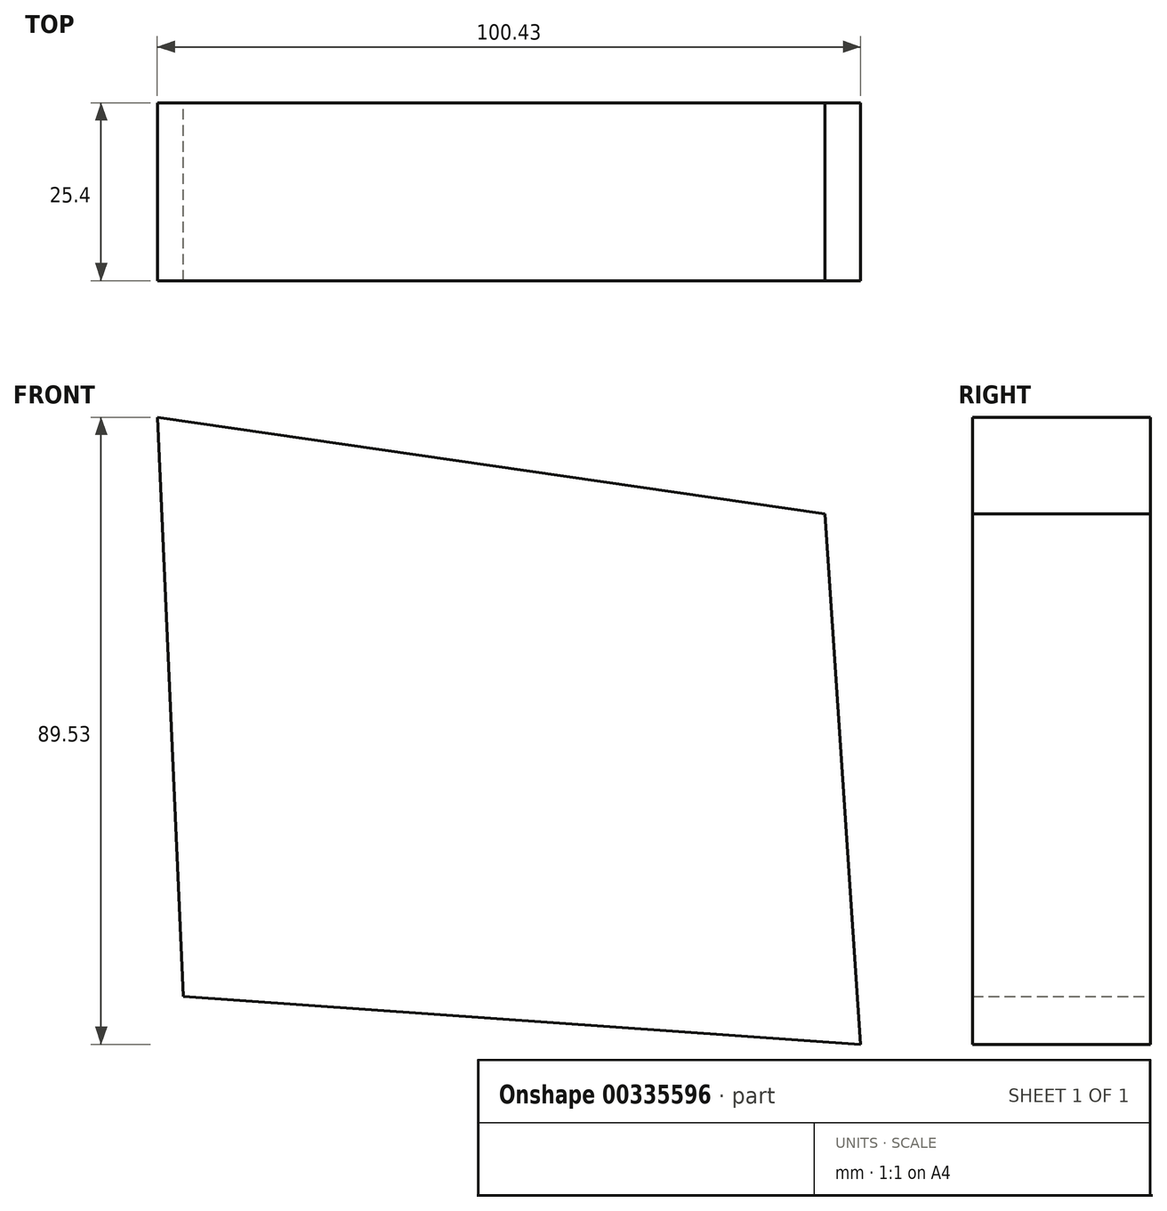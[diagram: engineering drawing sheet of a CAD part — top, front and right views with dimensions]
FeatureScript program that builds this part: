
annotation { "Feature Type Name" : "Feature", "Feature Type Description" : "" }
export const myFeature = defineFeature(function(context is Context, id is Id, definition is map)
    precondition{}
    {
        {
            var Q0;
            Q0=qCreatedBy(makeId("Front.planeOp"),FACE);
            var sketch = newSketch(context, id + "F0", { "sketchPlane" : qUnion([Q0])});
            skLineSegment(sketch, "E0", {"start": v(-48.03, 50.98) * mm, "end": v(-44.34, -31.73) * mm});
            skLineSegment(sketch, "E1", {"start": v(-44.34, -31.73) * mm, "end": v(52.4, -38.55) * mm});
            skLineSegment(sketch, "E2", {"start": v(52.4, -38.55) * mm, "end": v(47.32, 37.19) * mm});
            skLineSegment(sketch, "E3", {"start": v(47.32, 37.19) * mm, "end": v(-48.03, 50.98) * mm});
            skSolve(sketch);
        }
        {
            var Q0;
            Q0=makeQuery(id+"F0.imprint","IMPRINT",FACE,{"disambiguationData":[TD([[makeQuery(id+"F0.imprint","IMPRINT",EDGE,{"derivedFrom":sQuery(id+"F0.wireOp",EDGE,"E0")}),1.0]])]});
            var sketch = newSketch(context, id + "F1", { "sketchPlane" : qUnion([Q0])});
            skSolve(sketch);
        }
        {
            var Q0;
            Q0=makeQuery(id+"F1.imprint","IMPRINT",FACE,{"disambiguationData":[TD([[makeQuery(id+"F1.imprint","IMPRINT",EDGE,{"derivedFrom":makeQuery(id+"F0.imprint","IMPRINT",EDGE,{"derivedFrom":sQuery(id+"F0.wireOp",EDGE,"E0")})}),1.0]])]});
            extrude(context, id + "F2", {"entities" : qUnion([Q0]), "depth" : 25.4 * mm});
        }
    });
